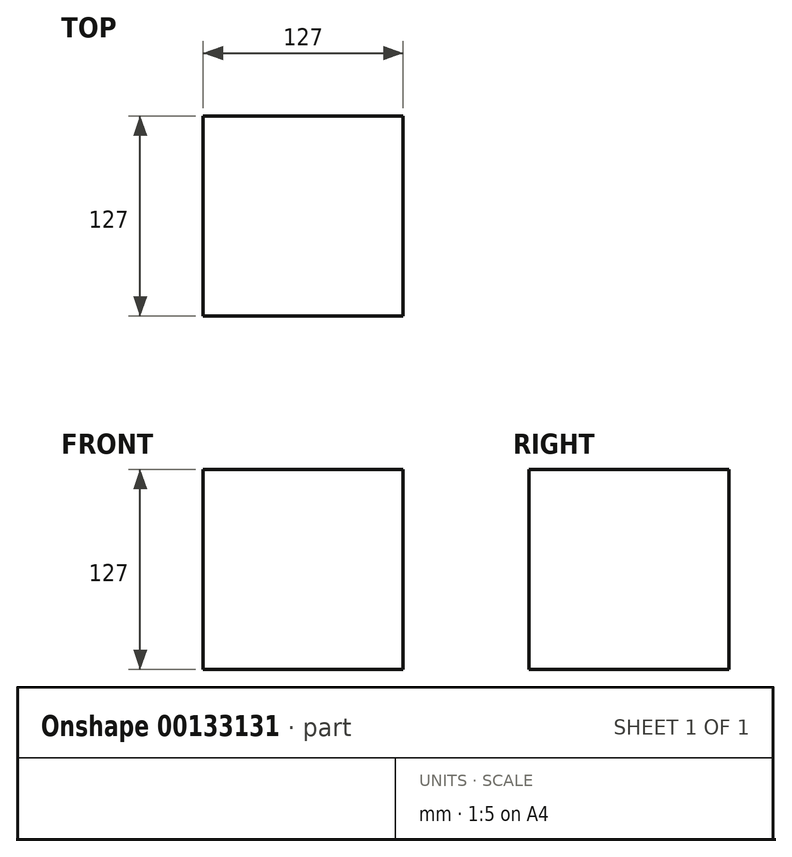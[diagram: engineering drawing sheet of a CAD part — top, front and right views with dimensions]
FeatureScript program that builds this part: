
annotation { "Feature Type Name" : "Feature", "Feature Type Description" : "" }
export const myFeature = defineFeature(function(context is Context, id is Id, definition is map)
    precondition{}
    {
        {
            var Q0;
            Q0=qCreatedBy(makeId("Front.planeOp"),FACE);
            var sketch = newSketch(context, id + "F0", { "sketchPlane" : qUnion([Q0])});
            skLineSegment(sketch, "E0.bottom", {"start": v(-63.5, -63.5) * mm, "end": v(63.5, -63.5) * mm});
            skLineSegment(sketch, "E0.top", {"start": v(-63.5, 63.5) * mm, "end": v(63.5, 63.5) * mm});
            skLineSegment(sketch, "E0.left", {"start": v(-63.5, -63.5) * mm, "end": v(-63.5, 63.5) * mm});
            skLineSegment(sketch, "E0.right", {"start": v(63.5, -63.5) * mm, "end": v(63.5, 63.5) * mm});
            skPoint(sketch, "E0.middle", {"position": v(0, 0) * mm});
            skSolve(sketch);
        }
        {
            var Q0;
            Q0=makeQuery(id+"F0.imprint","IMPRINT",FACE,{"disambiguationData":[TD([[makeQuery(id+"F0.imprint","IMPRINT",EDGE,{"derivedFrom":sQuery(id+"F0.wireOp",EDGE,"E0.bottom")}),1.0]])]});
            extrude(context, id + "F1", {"entities" : qUnion([Q0]), "endBound" : BoundingType.SYMMETRIC, "depth" : 127 * mm});
        }
    });
